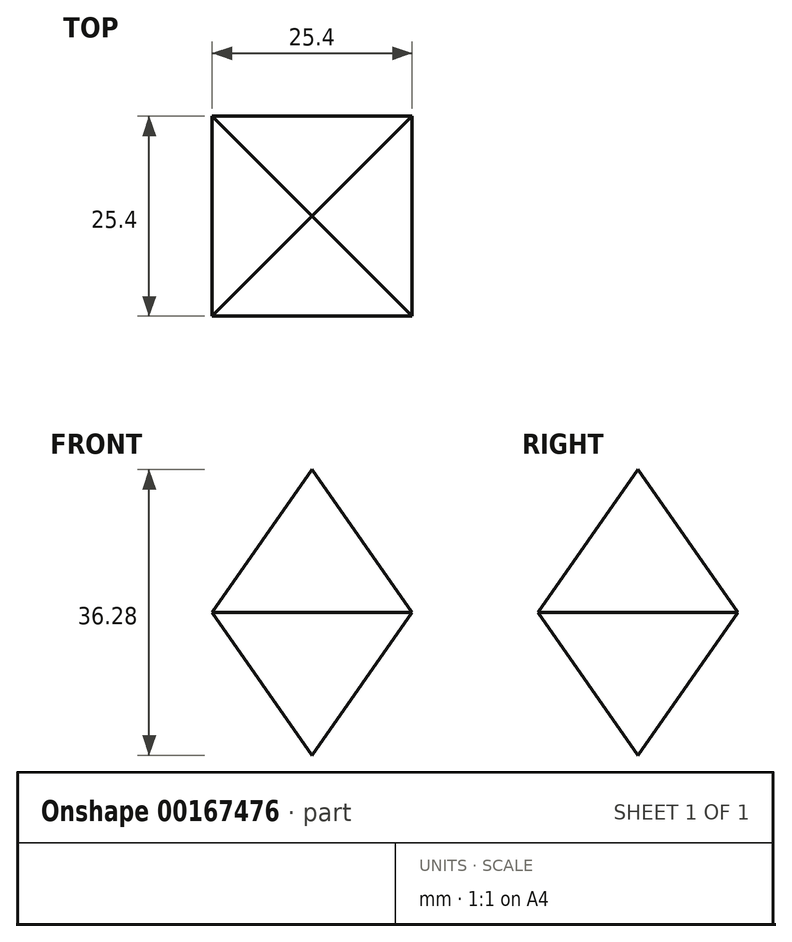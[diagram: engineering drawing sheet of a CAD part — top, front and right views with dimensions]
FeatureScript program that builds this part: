
annotation { "Feature Type Name" : "Feature", "Feature Type Description" : "" }
export const myFeature = defineFeature(function(context is Context, id is Id, definition is map)
    precondition{}
    {
        {
            var Q0;
            Q0=qCreatedBy(makeId("Top.planeOp"),FACE);
            var sketch = newSketch(context, id + "F0", { "sketchPlane" : qUnion([Q0])});
            skLineSegment(sketch, "E0.bottom", {"start": v(12.7, 12.7) * mm, "end": v(-12.7, 12.7) * mm});
            skLineSegment(sketch, "E0.top", {"start": v(12.7, -12.7) * mm, "end": v(-12.7, -12.7) * mm});
            skLineSegment(sketch, "E0.left", {"start": v(12.7, 12.7) * mm, "end": v(12.7, -12.7) * mm});
            skLineSegment(sketch, "E0.right", {"start": v(-12.7, 12.7) * mm, "end": v(-12.7, -12.7) * mm});
            skPoint(sketch, "E0.middle", {"position": v(0, 0) * mm});
            skSolve(sketch);
        }
        {
            var Q0;
            Q0 = qSketchRegion(id + "F0", true);
            var Q1;
            Q1=makeQuery(id+"F0.imprint","IMPRINT",FACE,{"disambiguationData":[TD([[makeQuery(id+"F0.imprint","IMPRINT",EDGE,{"derivedFrom":sQuery(id+"F0.wireOp",EDGE,"E0.bottom")}),1.0]])]});
            extrude(context, id + "F1", {"entities" : qUnion([Q0, Q1]), "depth" : 25.4 * mm, "hasDraft" : true, "draftAngle" : 35 * degree, "draftPullDirection" : true, "hasSecondDirection" : true, "secondDirectionOppositeDirection" : true, "secondDirectionDepth" : 25.4 * mm, "hasSecondDirectionDraft" : true, "secondDirectionDraftAngle" : 35 * degree, "secondDirectionDraftPullDirection" : true});
        }
    });
